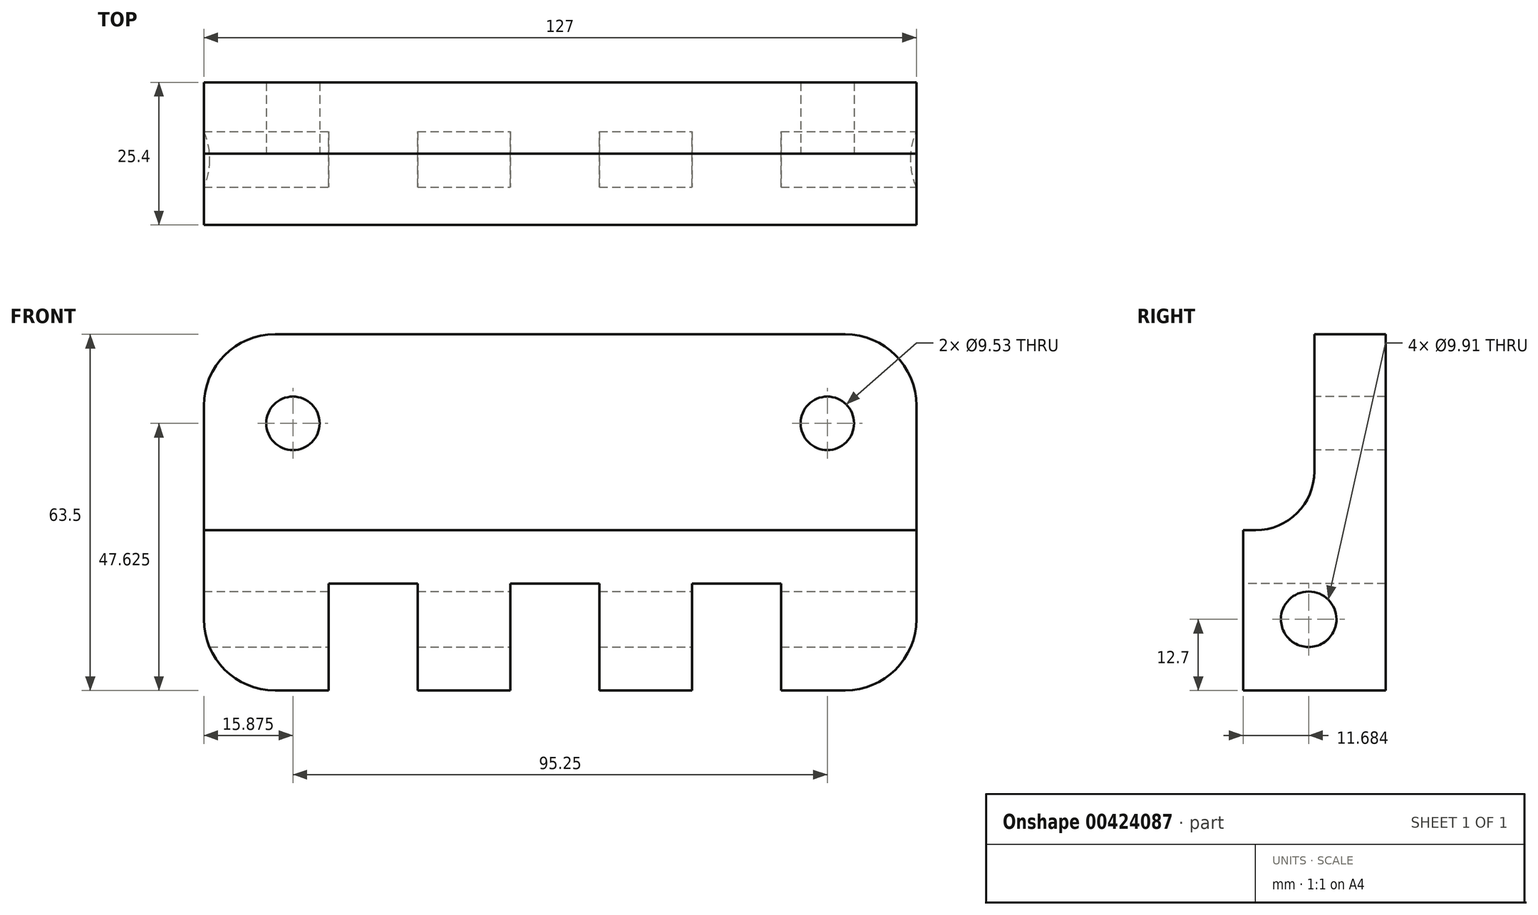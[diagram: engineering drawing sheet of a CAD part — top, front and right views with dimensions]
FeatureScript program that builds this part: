
annotation { "Feature Type Name" : "Feature", "Feature Type Description" : "" }
export const myFeature = defineFeature(function(context is Context, id is Id, definition is map)
    precondition{}
    {
        {
            var Q0;
            Q0=qCreatedBy(makeId("Right.planeOp"),FACE);
            var sketch = newSketch(context, id + "F0", { "sketchPlane" : qUnion([Q0])});
            skLineSegment(sketch, "E0.bottom", {"start": v(0, 0) * mm, "end": v(25.4, 0) * mm});
            skLineSegment(sketch, "E0.top", {"start": v(12.7, 63.5) * mm, "end": v(25.4, 63.5) * mm});
            skLineSegment(sketch, "E0.left", {"start": v(0, 0) * mm, "end": v(0, 28.58) * mm});
            skLineSegment(sketch, "E0.right", {"start": v(25.4, 0) * mm, "end": v(25.4, 63.5) * mm});
            skLineSegment(sketch, "E1", {"start": v(12.7, 63.5) * mm, "end": v(12.7, 39.05) * mm});
            skLineSegment(sketch, "E2", {"start": v(2.22, 28.58) * mm, "end": v(0, 28.58) * mm});
            skPoint(sketch, "E3.orphan", {"position": v(0, 63.5) * mm});
            skPoint(sketch, "E4.visualSharp", {"position": v(12.7, 28.58) * mm});
            skArc(sketch, "E4.filletArc", {"start": v(2.22, 28.58) * mm, "mid": v(9.63, 31.64) * mm, "end": v(12.7, 39.05) * mm});
            skSolve(sketch);
        }
        {
            var Q0;
            Q0 = qSketchRegion(id + "F0", true);
            extrude(context, id + "F1", {"entities" : qUnion([Q0]), "depth" : 127 * mm});
        }
        {
            var Q0;
            Q0=makeQuery(id+"F1.opExtrude","SWEPT_FACE",FACE,{"disambiguationData":[OSD([sQuery(id+"F0.wireOp",EDGE,"E1")])]});
            var sketch = newSketch(context, id + "F2", { "sketchPlane" : qUnion([Q0])});
            skLineSegment(sketch, "E5", {"start": v(127, 47.63) * mm, "end": v(111.12, 47.63) * mm});
            skCircle(sketch, "E6", {"center": v(111.12, 47.63) * mm, "radius": 4.76 * mm});
            skCircle(sketch, "E7", {"center": v(15.87, 47.62) * mm, "radius": 4.76 * mm});
            skSolve(sketch);
        }
        {
            var Q0;
            Q0 = qSketchRegion(id + "F2", true);
            extrude(context, id + "F3", {"entities" : qUnion([Q0]), "operationType" : NewBodyOperationType.REMOVE, "oppositeDirection" : true, "depth" : 25.4 * mm});
        }
        {
            var Q0;
            Q0=makeQuery(id+"F1.opExtrude","SWEPT_FACE",FACE,{"disambiguationData":[OSD([sQuery(id+"F0.wireOp",EDGE,"E0.left")])]});
            var sketch = newSketch(context, id + "F4", { "sketchPlane" : qUnion([Q0])});
            skLineSegment(sketch, "E8.bottom", {"start": v(102.87, 0) * mm, "end": v(87, 0) * mm});
            skLineSegment(sketch, "E8.top", {"start": v(102.87, 19.05) * mm, "end": v(87, 19.05) * mm});
            skLineSegment(sketch, "E8.left", {"start": v(102.87, 0) * mm, "end": v(102.87, 19.05) * mm});
            skLineSegment(sketch, "E8.right", {"start": v(87, 0) * mm, "end": v(87, 19.05) * mm});
            skLineSegment(sketch, "E9.bottom", {"start": v(70.48, 0) * mm, "end": v(54.6, 0) * mm});
            skLineSegment(sketch, "E9.top", {"start": v(70.48, 19.05) * mm, "end": v(54.6, 19.05) * mm});
            skLineSegment(sketch, "E9.left", {"start": v(70.48, 0) * mm, "end": v(70.48, 19.05) * mm});
            skLineSegment(sketch, "E9.right", {"start": v(54.6, 0) * mm, "end": v(54.6, 19.05) * mm});
            skLineSegment(sketch, "E10.bottom", {"start": v(38.1, 0) * mm, "end": v(22.22, 0) * mm});
            skLineSegment(sketch, "E10.top", {"start": v(38.1, 19.05) * mm, "end": v(22.22, 19.05) * mm});
            skLineSegment(sketch, "E10.left", {"start": v(38.1, 0) * mm, "end": v(38.1, 19.05) * mm});
            skLineSegment(sketch, "E10.right", {"start": v(22.22, 0) * mm, "end": v(22.22, 19.05) * mm});
            skSolve(sketch);
        }
        {
            var Q0;
            Q0 = qSketchRegion(id + "F4", true);
            extrude(context, id + "F5", {"entities" : qUnion([Q0]), "operationType" : NewBodyOperationType.REMOVE, "endBound" : BoundingType.THROUGH_ALL, "oppositeDirection" : true, "depth" : 25.4 * mm});
        }
        {
            var Q0;
            Q0=makeQuery(id+"F1.opExtrude","CAP_FACE",FACE,{"disambiguationData":[OSD([sQuery(id+"F0.wireOp",EDGE,"E0.bottom"),sQuery(id+"F0.wireOp",EDGE,"E0.top"),sQuery(id+"F0.wireOp",EDGE,"E0.left"),sQuery(id+"F0.wireOp",EDGE,"E0.right"),sQuery(id+"F0.wireOp",EDGE,"E1"),sQuery(id+"F0.wireOp",EDGE,"E2"),sQuery(id+"F0.wireOp",EDGE,"E4.filletArc")])],"isStart":false});
            var sketch = newSketch(context, id + "F6", { "sketchPlane" : qUnion([Q0])});
            skCircle(sketch, "E11", {"center": v(11.68, 12.7) * mm, "radius": 4.95 * mm});
            skSolve(sketch);
        }
        {
            var Q0;
            Q0 = qSketchRegion(id + "F6", true);
            extrude(context, id + "F7", {"entities" : qUnion([Q0]), "operationType" : NewBodyOperationType.REMOVE, "endBound" : BoundingType.THROUGH_ALL, "oppositeDirection" : true, "depth" : 25.4 * mm});
        }
        {
            var Q0;
            Q0=makeQuery(id+"F1.opExtrude","CAP_EDGE",EDGE,{"disambiguationData":[OSD([sQuery(id+"F0.wireOp",EDGE,"E0.top")])],"isStart":true});
            var Q1;
            Q1=makeQuery(id+"F1.opExtrude","CAP_EDGE",EDGE,{"disambiguationData":[OSD([sQuery(id+"F0.wireOp",EDGE,"E0.top")])],"isStart":false});
            var Q2;
            Q2=makeQuery(id+"F1.opExtrude","CAP_EDGE",EDGE,{"disambiguationData":[OSD([sQuery(id+"F0.wireOp",EDGE,"E0.bottom")])],"isStart":true});
            var Q3;
            Q3=makeQuery(id+"F1.opExtrude","CAP_EDGE",EDGE,{"disambiguationData":[OSD([sQuery(id+"F0.wireOp",EDGE,"E0.bottom")])],"isStart":false});
            fillet(context, id + "F8", {"entities" : qUnion([Q0, Q1, Q2, Q3]), "radius" : 12.7 * mm, "tangentPropagation" : true, "allowEdgeOverflow" : false});
        }
    });
